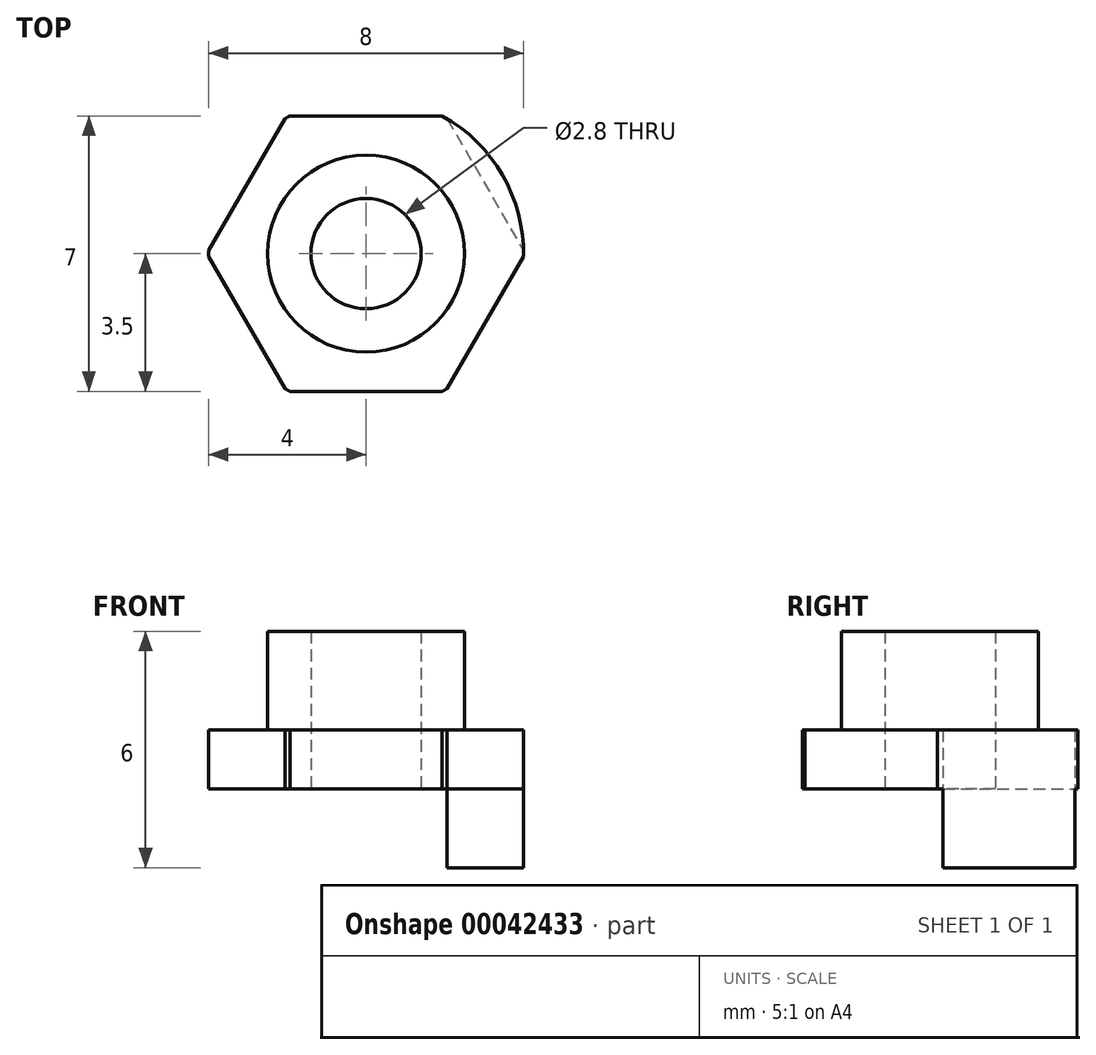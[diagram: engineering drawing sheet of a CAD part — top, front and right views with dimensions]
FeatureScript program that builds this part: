
annotation { "Feature Type Name" : "Feature", "Feature Type Description" : "" }
export const myFeature = defineFeature(function(context is Context, id is Id, definition is map)
    precondition{}
    {
        {
            var Q0;
            Q0=qCreatedBy(makeId("Top.planeOp"),FACE);
            var sketch = newSketch(context, id + "F0", { "sketchPlane" : qUnion([Q0])});
            skCircle(sketch, "E0", {"center": v(0, 0) * mm, "radius": 2.5 * mm});
            skCircle(sketch, "E1", {"center": v(0, 0) * mm, "radius": 1.4 * mm});
            skCircle(sketch, "E2", {"center": v(0, 0) * mm, "radius": 4 * mm});
            skCircle(sketch, "E3.cCircle", {"center": v(0, 0) * mm, "radius": 3.5 * mm, "construction": true});
            skLineSegment(sketch, "E3.0", {"start": v(4.04, 0) * mm, "end": v(2.02, -3.5) * mm});
            skLineSegment(sketch, "E3.1", {"start": v(2.02, -3.5) * mm, "end": v(-2.02, -3.5) * mm});
            skLineSegment(sketch, "E3.2", {"start": v(-2.02, -3.5) * mm, "end": v(-4.04, 0) * mm});
            skLineSegment(sketch, "E3.3", {"start": v(-4.04, 0) * mm, "end": v(-2.02, 3.5) * mm});
            skLineSegment(sketch, "E3.4", {"start": v(-2.02, 3.5) * mm, "end": v(2.02, 3.5) * mm});
            skLineSegment(sketch, "E3.5", {"start": v(2.02, 3.5) * mm, "end": v(4.04, 0) * mm});
            skPoint(sketch, "E3.0.midPoint", {"position": v(3.03, -1.75) * mm});
            skLineSegment(sketch, "E4", {"start": v(-7.3, 0) * mm, "end": v(8.92, 0) * mm, "construction": true});
            skSolve(sketch);
        }
        {
            var Q0;
            Q0=makeQuery(id+"F0.imprint","IMPRINT",FACE,{"disambiguationData":[TD([[makeQuery(id+"F0.imprint","IMPRINT",EDGE,{"derivedFrom":sQuery(id+"F0.wireOp",EDGE,"E0")}),1.0]])]});
            extrude(context, id + "F1", {"entities" : qUnion([Q0]), "depth" : 6 * mm});
        }
        {
            var Q0;
            Q0=makeQuery(id+"F0.imprint","IMPRINT",FACE,{"disambiguationData":[TD([[makeQuery(id+"F0.imprint","IMPRINT",EDGE,{"derivedFrom":sQuery(id+"F0.wireOp",EDGE,"E0")}),-1.0]])]});
            var Q1;
            {var subQ0=sQuery(id+"F0.wireOp",EDGE,"E3.4");var subQ1=sQuery(id+"F0.wireOp",EDGE,"E2");var subQ3=makeQuery(id+"F0.imprint","INTERSECT",VERTEX,{"disambiguationData":[OD(0.0)],"derivedFrom":[subQ1,subQ0]});Q1=makeQuery(id+"F0.imprint","IMPRINT",FACE,{"disambiguationData":[TD([[makeQuery(id+"F0.imprint","IMPRINT",EDGE,{"disambiguationData":[TD([[subQ3,-1.0]])],"derivedFrom":subQ1}),1.0]])]});}
            var Q2;
            {var subQ0=sQuery(id+"F0.wireOp",EDGE,"E3.3");var subQ1=sQuery(id+"F0.wireOp",EDGE,"E2");var subQ3=makeQuery(id+"F0.imprint","INTERSECT",VERTEX,{"disambiguationData":[OD(0.0)],"derivedFrom":[subQ1,subQ0]});Q2=makeQuery(id+"F0.imprint","IMPRINT",FACE,{"disambiguationData":[TD([[makeQuery(id+"F0.imprint","IMPRINT",EDGE,{"disambiguationData":[TD([[subQ3,-1.0]])],"derivedFrom":subQ1}),1.0]])]});}
            var Q3;
            {var subQ0=sQuery(id+"F0.wireOp",EDGE,"E3.2");var subQ1=sQuery(id+"F0.wireOp",EDGE,"E2");var subQ3=makeQuery(id+"F0.imprint","INTERSECT",VERTEX,{"disambiguationData":[OD(0.0)],"derivedFrom":[subQ1,subQ0]});Q3=makeQuery(id+"F0.imprint","IMPRINT",FACE,{"disambiguationData":[TD([[makeQuery(id+"F0.imprint","IMPRINT",EDGE,{"disambiguationData":[TD([[subQ3,-1.0]])],"derivedFrom":subQ1}),1.0]])]});}
            var Q4;
            {var subQ0=sQuery(id+"F0.wireOp",EDGE,"E3.1");var subQ1=sQuery(id+"F0.wireOp",EDGE,"E2");var subQ3=makeQuery(id+"F0.imprint","INTERSECT",VERTEX,{"disambiguationData":[OD(0.0)],"derivedFrom":[subQ1,subQ0]});Q4=makeQuery(id+"F0.imprint","IMPRINT",FACE,{"disambiguationData":[TD([[makeQuery(id+"F0.imprint","IMPRINT",EDGE,{"disambiguationData":[TD([[subQ3,-1.0]])],"derivedFrom":subQ1}),1.0]])]});}
            var Q5;
            {var subQ0=sQuery(id+"F0.wireOp",EDGE,"E3.0");var subQ1=sQuery(id+"F0.wireOp",EDGE,"E2");var subQ3=makeQuery(id+"F0.imprint","INTERSECT",VERTEX,{"disambiguationData":[OD(0.0)],"derivedFrom":[subQ1,subQ0]});Q5=makeQuery(id+"F0.imprint","IMPRINT",FACE,{"disambiguationData":[TD([[makeQuery(id+"F0.imprint","IMPRINT",EDGE,{"disambiguationData":[TD([[subQ3,-1.0]])],"derivedFrom":subQ1}),1.0]])]});}
            var Q6;
            {var subQ0=sQuery(id+"F0.wireOp",EDGE,"E3.5");var subQ1=sQuery(id+"F0.wireOp",EDGE,"E2");var subQ3=makeQuery(id+"F0.imprint","INTERSECT",VERTEX,{"disambiguationData":[OD(0.0)],"derivedFrom":[subQ1,subQ0]});Q6=makeQuery(id+"F0.imprint","IMPRINT",FACE,{"disambiguationData":[TD([[makeQuery(id+"F0.imprint","IMPRINT",EDGE,{"disambiguationData":[TD([[subQ3,1.0]])],"derivedFrom":subQ1}),1.0]])]});}
            extrude(context, id + "F2", {"entities" : qUnion([Q0, Q1, Q2, Q3, Q4, Q5, Q6]), "operationType" : NewBodyOperationType.ADD, "depth" : 3.5 * mm});
        }
        {
            var Q0;
            Q0=makeQuery(id+"F0.imprint","IMPRINT",FACE,{"disambiguationData":[TD([[makeQuery(id+"F0.imprint","IMPRINT",EDGE,{"derivedFrom":sQuery(id+"F0.wireOp",EDGE,"E0")}),-1.0]])]});
            var Q1;
            Q1=makeQuery(id+"F0.imprint","IMPRINT",FACE,{"disambiguationData":[TD([[makeQuery(id+"F0.imprint","IMPRINT",EDGE,{"derivedFrom":sQuery(id+"F0.wireOp",EDGE,"E0")}),1.0]])]});
            extrude(context, id + "F3", {"entities" : qUnion([Q0, Q1]), "operationType" : NewBodyOperationType.REMOVE, "depth" : 2 * mm});
        }
    });
